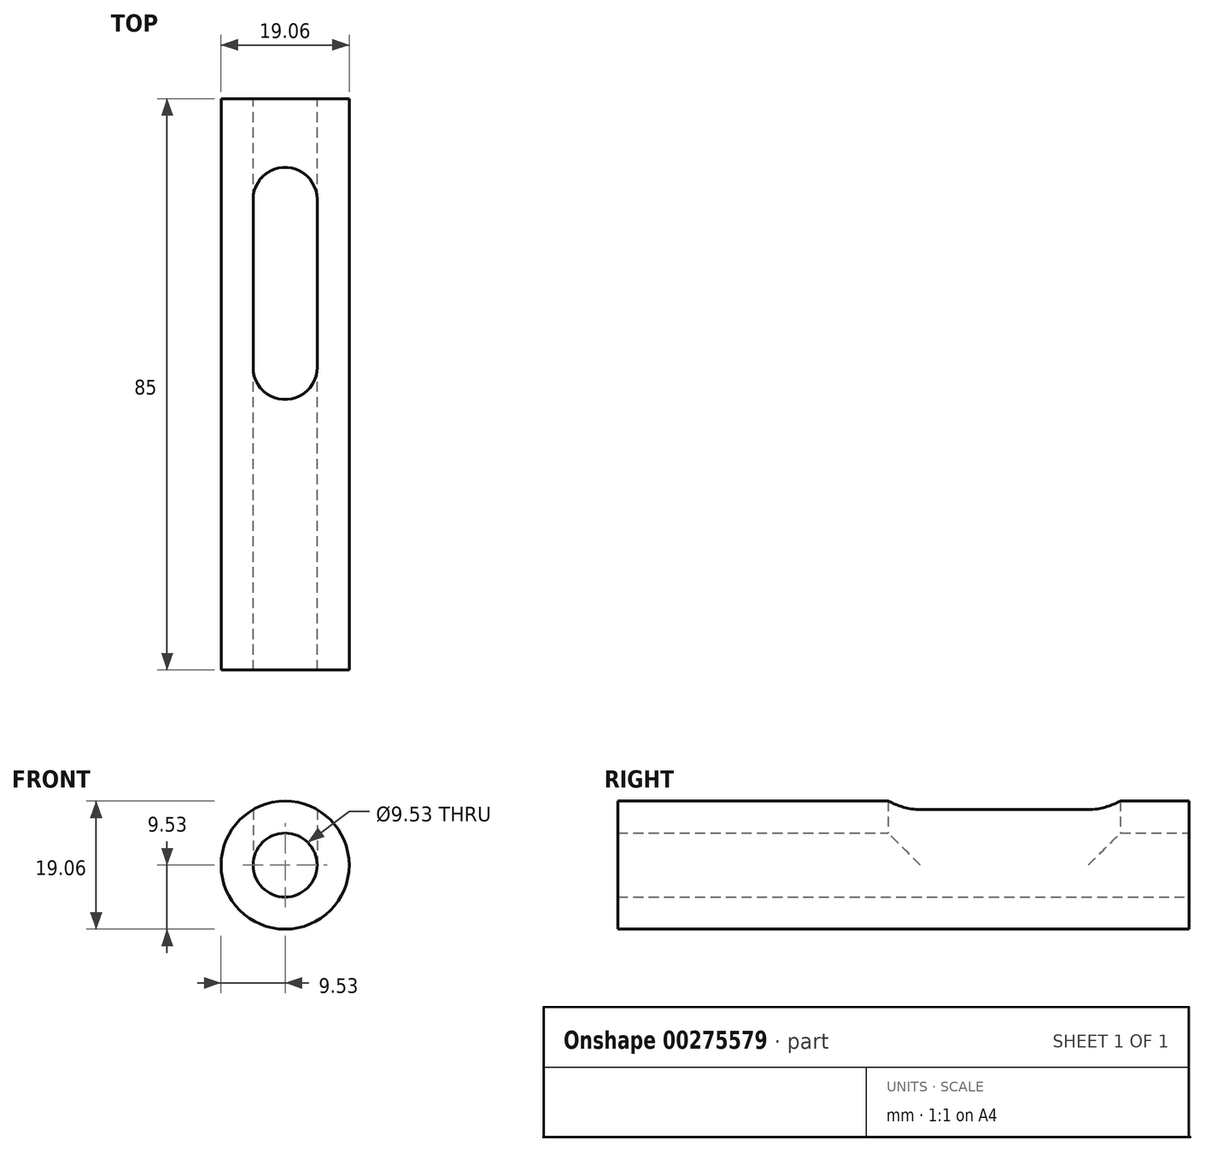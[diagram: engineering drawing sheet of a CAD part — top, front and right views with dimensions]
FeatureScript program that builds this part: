
annotation { "Feature Type Name" : "Feature", "Feature Type Description" : "" }
export const myFeature = defineFeature(function(context is Context, id is Id, definition is map)
    precondition{}
    {
        {
            var Q0;
            Q0=qCreatedBy(makeId("Front.planeOp"),FACE);
            var sketch = newSketch(context, id + "F0", { "sketchPlane" : qUnion([Q0])});
            skCircle(sketch, "E0", {"center": v(0, 0) * mm, "radius": 4.76 * mm});
            skCircle(sketch, "E1", {"center": v(0, 0) * mm, "radius": 9.53 * mm});
            skSolve(sketch);
        }
        {
            var Q0;
            Q0 = qSketchRegion(id + "F0", true);
            extrude(context, id + "F1", {"entities" : qUnion([Q0]), "depth" : 85 * mm});
        }
        {
            var Q0;
            Q0=qCreatedBy(makeId("Top.planeOp"),FACE);
            var sketch = newSketch(context, id + "F2", { "sketchPlane" : qUnion([Q0])});
            skLineSegment(sketch, "E2", {"start": v(0, 0) * mm, "end": v(0, -40) * mm, "construction": true});
            skLineSegment(sketch, "E3.bottom", {"start": v(-4.76, -15) * mm, "end": v(4.76, -15) * mm});
            skLineSegment(sketch, "E3.top", {"start": v(-4.76, -40) * mm, "end": v(4.76, -40) * mm});
            skLineSegment(sketch, "E3.left", {"start": v(-4.76, -15) * mm, "end": v(-4.76, -40) * mm});
            skLineSegment(sketch, "E3.right", {"start": v(4.76, -15) * mm, "end": v(4.76, -40) * mm});
            skCircle(sketch, "E4", {"center": v(0, -40) * mm, "radius": 4.76 * mm});
            skCircle(sketch, "E5", {"center": v(0, -15) * mm, "radius": 4.76 * mm});
            skSolve(sketch);
        }
        {
            var Q0;
            Q0 = qSketchRegion(id + "F2", true);
            extrude(context, id + "F3", {"entities" : qUnion([Q0]), "operationType" : NewBodyOperationType.REMOVE, "endBound" : BoundingType.THROUGH_ALL, "depth" : 25 * mm});
        }
    });
